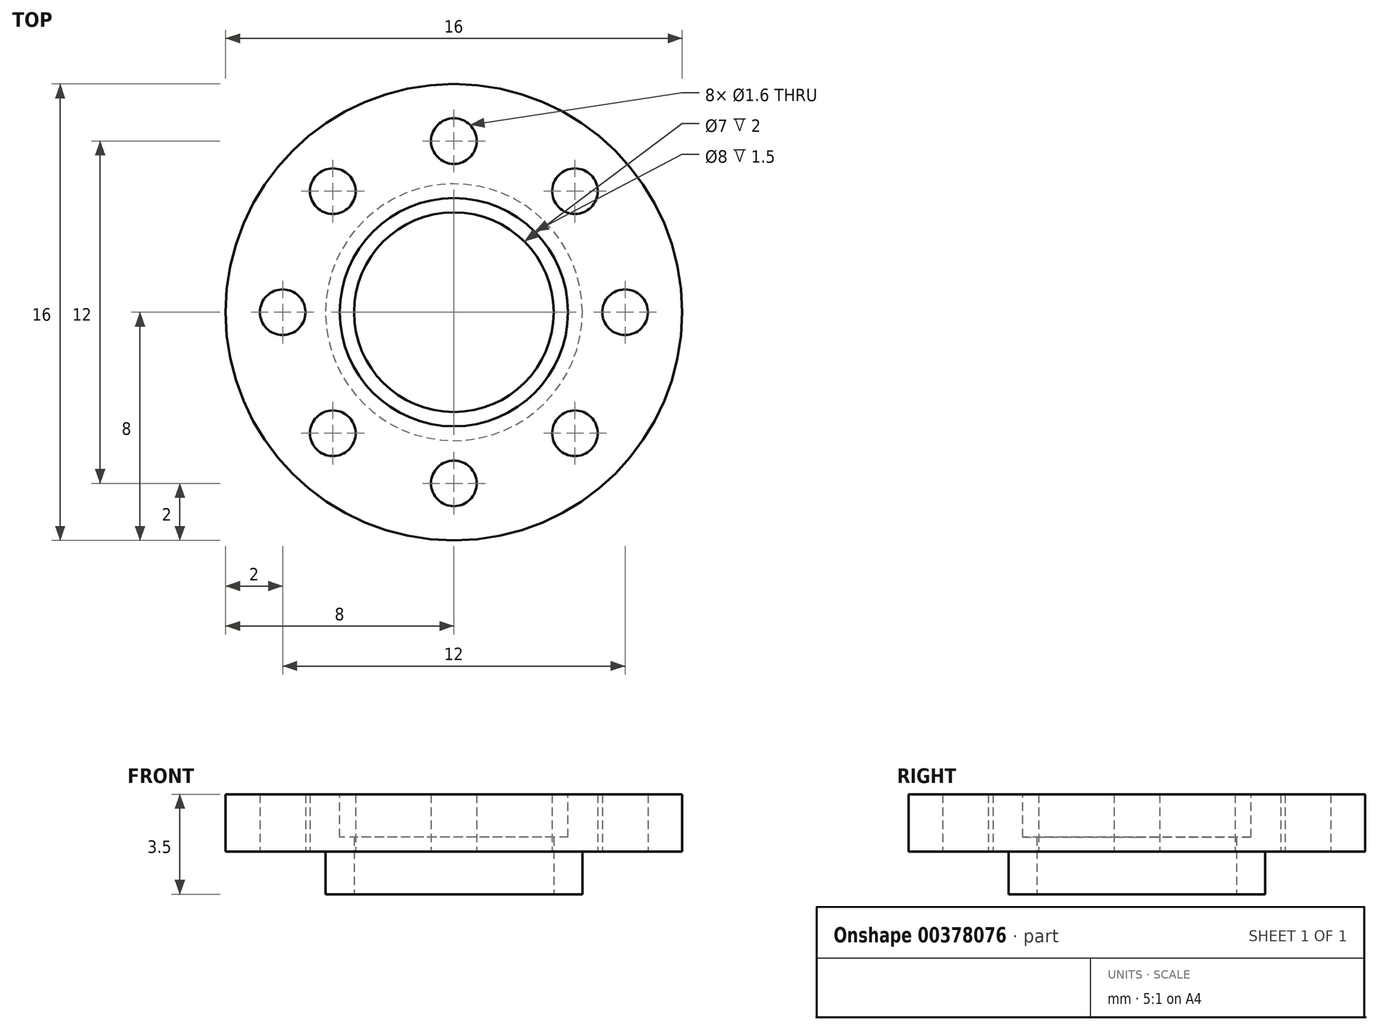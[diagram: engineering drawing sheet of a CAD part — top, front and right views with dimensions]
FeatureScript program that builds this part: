
annotation { "Feature Type Name" : "Feature", "Feature Type Description" : "" }
export const myFeature = defineFeature(function(context is Context, id is Id, definition is map)
    precondition{}
    {
        {
            var Q0;
            Q0=qCreatedBy(makeId("Top.planeOp"),FACE);
            var sketch = newSketch(context, id + "F0", { "sketchPlane" : qUnion([Q0])});
            skCircle(sketch, "E0", {"center": v(0, 0) * mm, "radius": 3.5 * mm});
            skCircle(sketch, "E1", {"center": v(0, 0) * mm, "radius": 4.5 * mm});
            skSolve(sketch);
        }
        {
            var Q0;
            Q0=makeQuery(id+"F0.imprint","IMPRINT",FACE,{"disambiguationData":[TD([[makeQuery(id+"F0.imprint","IMPRINT",EDGE,{"derivedFrom":sQuery(id+"F0.wireOp",EDGE,"E0")}),-1.0]])]});
            extrude(context, id + "F1", {"entities" : qUnion([Q0]), "depth" : 1.5 * mm});
        }
        {
            var Q0;
            Q0=makeQuery(id+"F1.opExtrude","CAP_FACE",FACE,{"disambiguationData":[OSD([sQuery(id+"F0.wireOp",EDGE,"E0"),sQuery(id+"F0.wireOp",EDGE,"E1")])],"isStart":false});
            var sketch = newSketch(context, id + "F2", { "sketchPlane" : qUnion([Q0])});
            skCircle(sketch, "E2", {"center": v(0, 0) * mm, "radius": 8 * mm});
            skCircle(sketch, "E3.0", {"center": v(0, 0) * mm, "radius": 3.5 * mm});
            skLineSegment(sketch, "E4", {"start": v(0, 0) * mm, "end": v(0, 6) * mm, "construction": true});
            skCircle(sketch, "E5", {"center": v(0, 6) * mm, "radius": 0.8 * mm});
            skCircle(sketch, "E6.1.0", {"center": v(-4.24, 4.24) * mm, "radius": 0.8 * mm});
            skCircle(sketch, "E6.2.0", {"center": v(-6, 0) * mm, "radius": 0.8 * mm});
            skCircle(sketch, "E6.3.0", {"center": v(-4.24, -4.24) * mm, "radius": 0.8 * mm});
            skCircle(sketch, "E6.4.0", {"center": v(0, -6) * mm, "radius": 0.8 * mm});
            skCircle(sketch, "E6.5.0", {"center": v(4.24, -4.24) * mm, "radius": 0.8 * mm});
            skCircle(sketch, "E6.6.0", {"center": v(6, 0) * mm, "radius": 0.8 * mm});
            skCircle(sketch, "E6.7.0", {"center": v(4.24, 4.24) * mm, "radius": 0.8 * mm});
            skSolve(sketch);
        }
        {
            var Q0;
            Q0=makeQuery(id+"F2.imprint","IMPRINT",FACE,{"disambiguationData":[TD([[makeQuery(id+"F2.imprint","IMPRINT",EDGE,{"derivedFrom":sQuery(id+"F2.wireOp",EDGE,"E3.0")}),-1.0]])]});
            var Q1;
            Q1=makeQuery(id+"F2.imprint","IMPRINT",FACE,{"disambiguationData":[TD([[makeQuery(id+"F2.imprint","IMPRINT",EDGE,{"derivedFrom":sQuery(id+"F2.wireOp",EDGE,"E2")}),1.0]])]});
            extrude(context, id + "F3", {"entities" : qUnion([Q0, Q1]), "operationType" : NewBodyOperationType.ADD, "depth" : 2 * mm});
        }
        {
            var Q0;
            Q0=makeQuery(id+"F3.opExtrude","CAP_FACE",FACE,{"disambiguationData":[OSD([sQuery(id+"F2.wireOp",EDGE,"E2"),sQuery(id+"F2.wireOp",EDGE,"E3.0"),sQuery(id+"F2.wireOp",EDGE,"E5"),sQuery(id+"F2.wireOp",EDGE,"E6.1.0"),sQuery(id+"F2.wireOp",EDGE,"E6.2.0"),sQuery(id+"F2.wireOp",EDGE,"E6.3.0"),sQuery(id+"F2.wireOp",EDGE,"E6.4.0"),sQuery(id+"F2.wireOp",EDGE,"E6.5.0"),sQuery(id+"F2.wireOp",EDGE,"E6.6.0"),sQuery(id+"F2.wireOp",EDGE,"E6.7.0")])],"isStart":false});
            var sketch = newSketch(context, id + "F4", { "sketchPlane" : qUnion([Q0])});
            skCircle(sketch, "E7", {"center": v(0, 0) * mm, "radius": 4 * mm});
            skSolve(sketch);
        }
        {
            var Q0;
            Q0=qSketchRegion(id+"F4",true);
            extrude(context, id + "F5", {"entities" : qUnion([Q0]), "operationType" : NewBodyOperationType.REMOVE, "oppositeDirection" : true, "depth" : 1.5 * mm});
        }
    });
